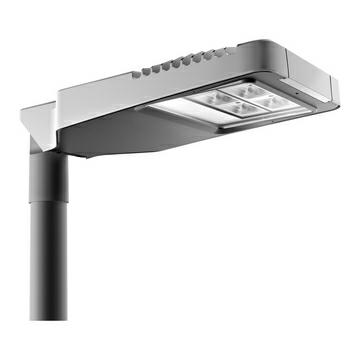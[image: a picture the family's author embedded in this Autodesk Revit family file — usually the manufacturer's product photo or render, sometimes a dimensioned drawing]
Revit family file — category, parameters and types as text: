
# Revit family: Lighting-StreetLighting-GEWISS-ROAD[5]MEDIUM-LED_OPTIC_WIDE-W_CLI
name_source: partatom
category: Apparecchi per illuminazione
units: mm (PartAtom-declared; Revit-internal decimal feet)

## family parameters
Basato su piano di lavoro = No
Condiviso = No
Punto di calcolo locali = No
Quota connettore circolare = Usa diametro
Sempre verticale = Sì
Sorgente d'illuminazione = No
Taglio con vuoti quando caricato = No
Tipo di parte = Normale

## types (5) — shared parameters
Applicazione = External
Body = Die-cast aluminium -
Catalogue = LIGHTING
Catalogue Range = ROAD [5]
Classification: = -
Color Rendering Index = CRI-70
Colore = Graphite grey
Colour : = Powder coating
Colour temperature = 4000K
Colour temperature: = 4000 K (CRI>70)
Context = Street and parking lighting
Control System = Bi-power with self-learning
DIN 18032-3 certification = -
Device with reduced surface temperature = -
Driver = Included
Driver Box = Built-in
Electrocod = 244C
Eletrical and lighting features = -
External screw = Stainless steel
Fixing = Pole Head - Outreach
Gasket = Anti-aging silicone
General information = -
Glow Wire Test : = -
IDF = f55c7619-358d-4cb2-a14f-db6071f73c56
IDT = 9b7d0eba829245cc99b21f64ea3ca485
IP degree = IP66
Immagine tipo = GWR5276M.jpg
Installationa and maintenance = -
Insulation class = II
LED Life time (L80B10) = 100000H
LED Maintenance = Not available
Lamp- = LED
Lampada = LED
Lifetime = L90B10 (Tq+25°C) = 100.000 h
Locking Hook = Integrated front handle
Luminaire = LED Road Equipment
Materials = -
Maximum surface exposed to the wind = 0,19M2
Maximum surface exposed to the wind : = 0.19 m2
Minimum distance from the illuminated object = 1M
Mouting and installation = Pole Head - Outreach
Optic = WIDE
Optic : = Metallized polycarbonate reflector
Optic Maintenance = Not available
Optic and illuminating features = -
Overvoltage protection = DM 10KV / CM 10KV
Overvoltage resistance = 10 KV (Common mode)
Photobiological Risk Class = RG0
Produttore = GEWISS S.p.A.
Rated frequency (Hz) = 50 / 60
SEO = Street lighting
Shield type = 4mm thick flat tempered glass
Shock resistance = IK08
Standard Deviation Colour Matching = SDCM = 5
Standard- = EN 60598-2-3, EN 60598-1 IEC/TR 62778
Standards and approvals = -
Stocking temperature = -
Supply voltage = 220 - 240 V
Technical sheet = https://www.gewiss.com
Tilt adjustable = -20° ÷ +10° side bracket - -10° ÷ +20° pole head
Tilt- = -20° ÷ +10° side bracket - -10° ÷ +20° pole head
Tipo alimentatore = Constant Current Driver Led
Tipologia = Bi power
Type of light source = LED - Not replaceable
URL = https://www.gewiss.com
Unified Glare Rating = G*4 - ULOR = 0
Unique digital code (Datamatrix) = Currently not present
Version file RFA = 20.11
Voltage- = 220 / 240 V - 50 / 60 Hz
Warranty = 5 years
Wiring = Isolating switch

## per-type parameters (varying)
| type | Efficiency (lm/W) | IPEA | LED current. | Lumen output (lm) | Modello | Number of modules | Operating temperature : | Operating temperature: | System power | System power : | Weight (kg): |
| GWR5254BW - ROAD5 MEDI WIDE 4M 4000K 0,50A CL2 BI.W | 110 | ROAD = A + // LARGE AREAS = A4 + // CYCLOPEDONALS = A + // GREEN AREAS = A + // HISTORICAL CENTER = A5 + | 0,5A | 16100 | GWR5254BW | 4 (4x3 LED) | -25 +30 °C | -25 +30 °C | 146W | 146 W @ 0.5A | 8,4 |
| GWR5234BW - ROAD5 MEDI WIDE 4M 4000K 0,35A CL2 BI.W | 120 | ROAD = A3 + // LARGE AREAS = A6 + // CYCLOPEDONALS = A3 + // GREEN AREAS = A3 + // HISTORICAL CENTER = A6 + | 0,35A | 12000 | GWR5234BW | 4 (4x3 LED) | -25 +40 °C | -25 +40 °C | 100W | 100 W @ 0.35A | 8,4 |
| GWR5233BW - ROAD5 MEDI WIDE 3M 4000K 0,35A CL2 BI.W | 120 | ROAD = A4 + // LARGE AREAS = A6 + // CYCLOPEDONALS = A3 + // GREEN AREAS = A3 + // HISTORICAL CENTER = A6 + | 0,35A | 9100 | GWR5233BW | 3 (3x3 LED) | -25 +40 °C | -25 +40 °C | 76W | 76 W @ 0.35A | 8 |
| GWR5253BW - ROAD5 MEDI WIDE 3M 4000K 0,50A CL2 BI.W | 112 | ROAD = A ++ // LARGE AREAS = A4 + // CYCLOPEDONALS = A ++ // GREEN AREAS = A ++ // HISTORICAL CENTER = A6 + | 0,5A | 12200 | GWR5253BW | 3 (3x3 LED) | -25 +30 °C | -25 +30 °C | 109W | 109 W @ 0.5A | 8 |
| GWR5235BW - ROAD5 MEDI WIDE 5M 4000K 0,35A CL2 BI.W | 120 | ROAD = A ++ // LARGE AREAS = A5 + // CYCLOPEDONALS = A ++ // GREEN AREAS = A ++ // HISTORICAL CENTER = A6 + | 0,35A | 15000 | GWR5235BW | 5 (5x3 LED) | -25 +40 °C | -25 +40 °C | 125W | 125 W @ 0.35A | 8,8 |

note: column(s) folded — value = type name in every type: Descrizione

## geometry (parser evidence)
native form markers: Blend x2
no freeform markers — native parametric forms only
